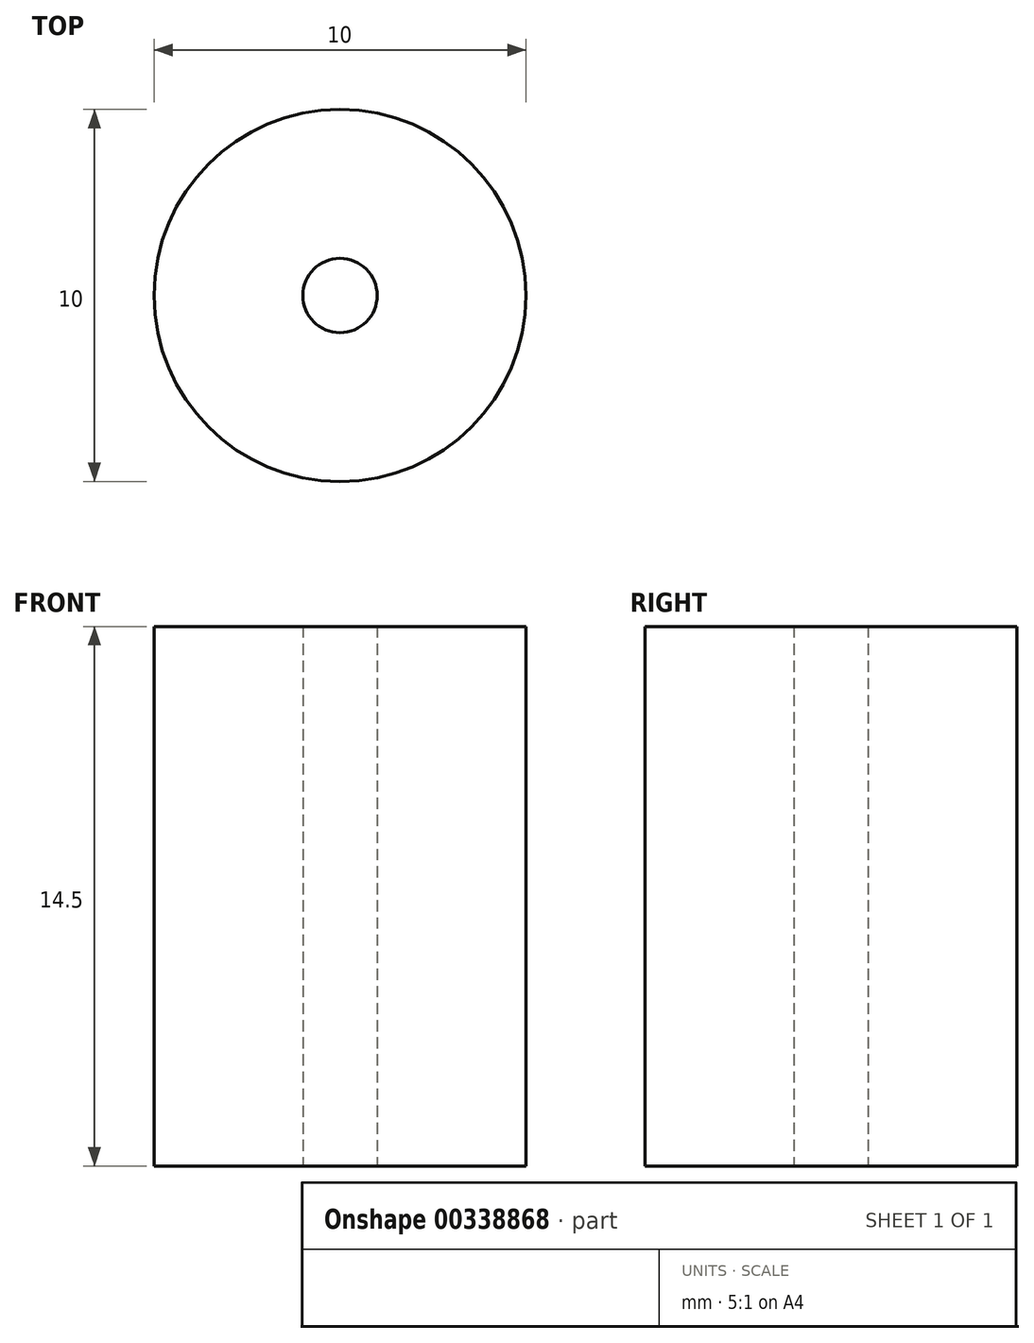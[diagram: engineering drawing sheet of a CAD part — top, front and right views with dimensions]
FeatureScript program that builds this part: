
annotation { "Feature Type Name" : "Feature", "Feature Type Description" : "" }
export const myFeature = defineFeature(function(context is Context, id is Id, definition is map)
    precondition{}
    {
        {
            var Q0;
            Q0=qCreatedBy(makeId("Top.planeOp"),FACE);
            var sketch = newSketch(context, id + "F0", { "sketchPlane" : qUnion([Q0])});
            skCircle(sketch, "E0", {"center": v(0, 0) * mm, "radius": 5 * mm});
            skCircle(sketch, "E1", {"center": v(0, 0) * mm, "radius": 1 * mm});
            skSolve(sketch);
        }
        {
            var Q0;
            Q0 = qSketchRegion(id + "F0", true);
            extrude(context, id + "F1", {"entities" : qUnion([Q0]), "depth" : 14.5 * mm});
        }
    });
